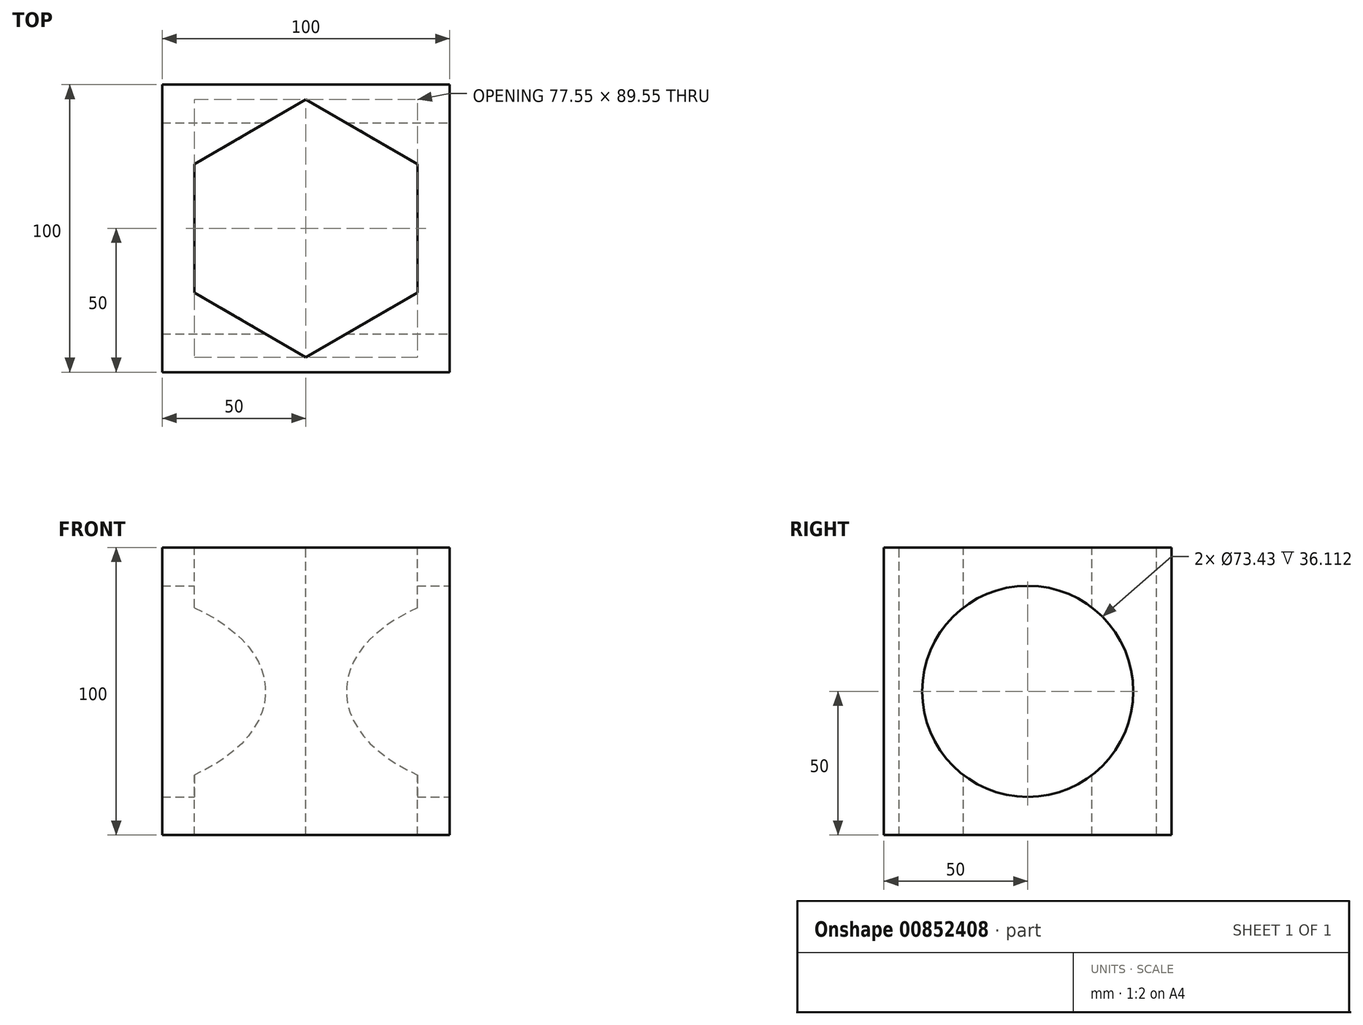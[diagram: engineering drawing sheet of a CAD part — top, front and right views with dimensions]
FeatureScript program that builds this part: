
annotation { "Feature Type Name" : "Feature", "Feature Type Description" : "" }
export const myFeature = defineFeature(function(context is Context, id is Id, definition is map)
    precondition{}
    {
        {
            var Q0;
            Q0=qCreatedBy(makeId("Right.planeOp"),FACE);
            var sketch = newSketch(context, id + "F0", { "sketchPlane" : qUnion([Q0])});
            skLineSegment(sketch, "E0.bottom", {"start": v(0, 0) * mm, "end": v(100, 0) * mm});
            skLineSegment(sketch, "E0.top", {"start": v(0, 100) * mm, "end": v(100, 100) * mm});
            skLineSegment(sketch, "E0.left", {"start": v(0, 0) * mm, "end": v(0, 100) * mm});
            skLineSegment(sketch, "E0.right", {"start": v(100, 0) * mm, "end": v(100, 100) * mm});
            skSolve(sketch);
        }
        {
            var Q0;
            Q0 = qSketchRegion(id + "F0", true);
            extrude(context, id + "F1", {"entities" : qUnion([Q0]), "depth" : 100 * mm, "offsetDistance" : 25 * mm});
        }
        {
            var Q0;
            Q0=makeQuery(id+"F1.opExtrude","CAP_FACE",FACE,{"disambiguationData":[OSD([sQuery(id+"F0.wireOp",EDGE,"E0.bottom"),sQuery(id+"F0.wireOp",EDGE,"E0.top"),sQuery(id+"F0.wireOp",EDGE,"E0.left"),sQuery(id+"F0.wireOp",EDGE,"E0.right")])],"isStart":false});
            var sketch = newSketch(context, id + "F2", { "sketchPlane" : qUnion([Q0])});
            skCircle(sketch, "E1", {"center": v(50, 50) * mm, "radius": 36.72 * mm});
            skPoint(sketch, "E1.centerSnap0", {"position": v(50, 100) * mm});
            skPoint(sketch, "E1.centerSnap1", {"position": v(0, 50) * mm});
            skSolve(sketch);
        }
        {
            var Q0;
            Q0=makeQuery(id+"F2.imprint","IMPRINT",FACE,{"disambiguationData":[TD([[makeQuery(id+"F2.imprint","IMPRINT",EDGE,{"derivedFrom":sQuery(id+"F2.wireOp",EDGE,"E1")}),1.0]])]});
            var Q1;
            Q1=sQuery(id+"F2.wireOp",EDGE,"E1");
            extrude(context, id + "F3", {"entities" : qUnion([Q0]), "operationType" : NewBodyOperationType.REMOVE, "surfaceEntities" : qUnion([Q1]), "endBound" : BoundingType.UP_TO_NEXT, "oppositeDirection" : true, "depth" : 25 * mm, "offsetDistance" : 25 * mm});
        }
        {
            var Q0;
            Q0=makeQuery(id+"F1.opExtrude","SWEPT_FACE",FACE,{"disambiguationData":[OSD([sQuery(id+"F0.wireOp",EDGE,"E0.top")])]});
            var sketch = newSketch(context, id + "F4", { "sketchPlane" : qUnion([Q0])});
            skCircle(sketch, "E2.cCircle", {"center": v(50, 50) * mm, "radius": 38.78 * mm, "construction": true});
            skPoint(sketch, "E2.cCircle.centerSnap0", {"position": v(50, 100) * mm});
            skPoint(sketch, "E2.cCircle.centerSnap1", {"position": v(0, 50) * mm});
            skLineSegment(sketch, "E2.0", {"start": v(88.78, 72.39) * mm, "end": v(88.78, 27.61) * mm});
            skLineSegment(sketch, "E2.1", {"start": v(88.78, 27.61) * mm, "end": v(50, 5.22) * mm});
            skLineSegment(sketch, "E2.2", {"start": v(50, 5.22) * mm, "end": v(11.22, 27.61) * mm});
            skLineSegment(sketch, "E2.3", {"start": v(11.22, 27.61) * mm, "end": v(11.22, 72.39) * mm});
            skLineSegment(sketch, "E2.4", {"start": v(11.22, 72.39) * mm, "end": v(50, 94.78) * mm});
            skLineSegment(sketch, "E2.5", {"start": v(50, 94.78) * mm, "end": v(88.78, 72.39) * mm});
            skPoint(sketch, "E2.0.midPoint", {"position": v(88.78, 50) * mm});
            skSolve(sketch);
        }
        {
            var Q0;
            Q0=makeQuery(id+"F4.imprint","IMPRINT",FACE,{"disambiguationData":[TD([[makeQuery(id+"F4.imprint","IMPRINT",EDGE,{"derivedFrom":sQuery(id+"F4.wireOp",EDGE,"E2.0")}),-1.0]])]});
            extrude(context, id + "F5", {"entities" : qUnion([Q0]), "operationType" : NewBodyOperationType.REMOVE, "endBound" : BoundingType.THROUGH_ALL, "oppositeDirection" : true, "depth" : 25 * mm, "offsetDistance" : 25 * mm});
        }
    });
